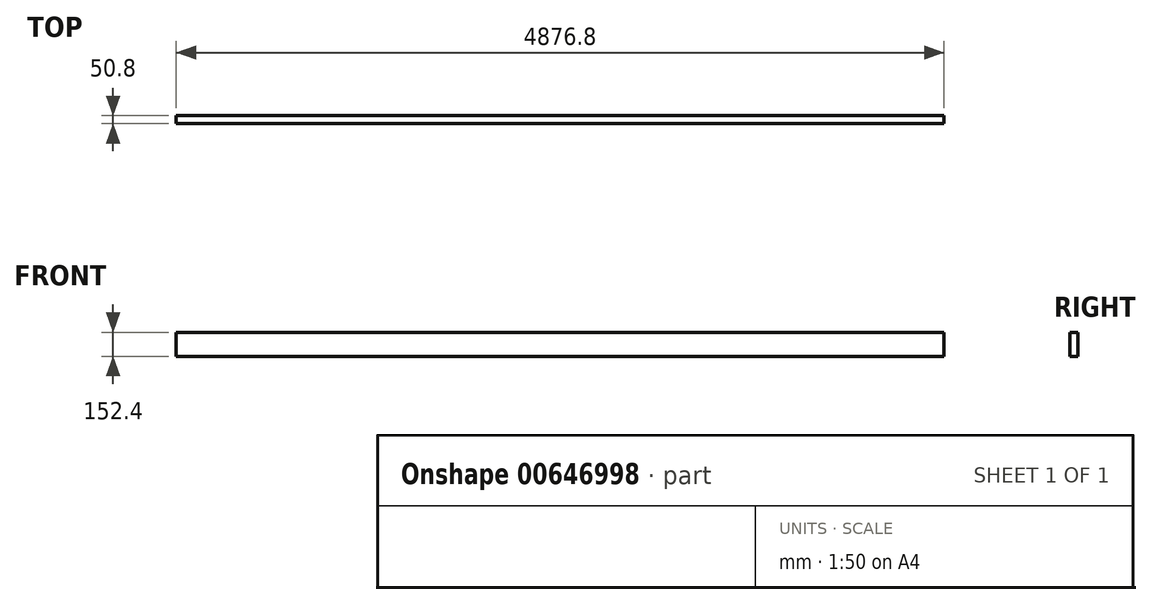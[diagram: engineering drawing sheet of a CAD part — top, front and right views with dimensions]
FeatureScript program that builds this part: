
annotation { "Feature Type Name" : "Feature", "Feature Type Description" : "" }
export const myFeature = defineFeature(function(context is Context, id is Id, definition is map)
    precondition{}
    {
        {
            var Q0;
            Q0=qCreatedBy(makeId("Front.planeOp"),FACE);
            var sketch = newSketch(context, id + "F0", { "sketchPlane" : qUnion([Q0])});
            skLineSegment(sketch, "E0.bottom", {"start": v(-2437.17, -65.77) * mm, "end": v(2439.63, -65.77) * mm});
            skLineSegment(sketch, "E0.top", {"start": v(-2437.17, -218.17) * mm, "end": v(2439.63, -218.17) * mm});
            skLineSegment(sketch, "E0.left", {"start": v(-2437.17, -65.77) * mm, "end": v(-2437.17, -218.17) * mm});
            skLineSegment(sketch, "E0.right", {"start": v(2439.63, -65.77) * mm, "end": v(2439.63, -218.17) * mm});
            skSolve(sketch);
        }
        {
            var Q0;
            Q0 = qSketchRegion(id + "F0", true);
            extrude(context, id + "F1", {"entities" : qUnion([Q0]), "endBound" : BoundingType.SYMMETRIC, "depth" : 50.8 * mm, "offsetDistance" : 25.4 * mm});
        }
    });
